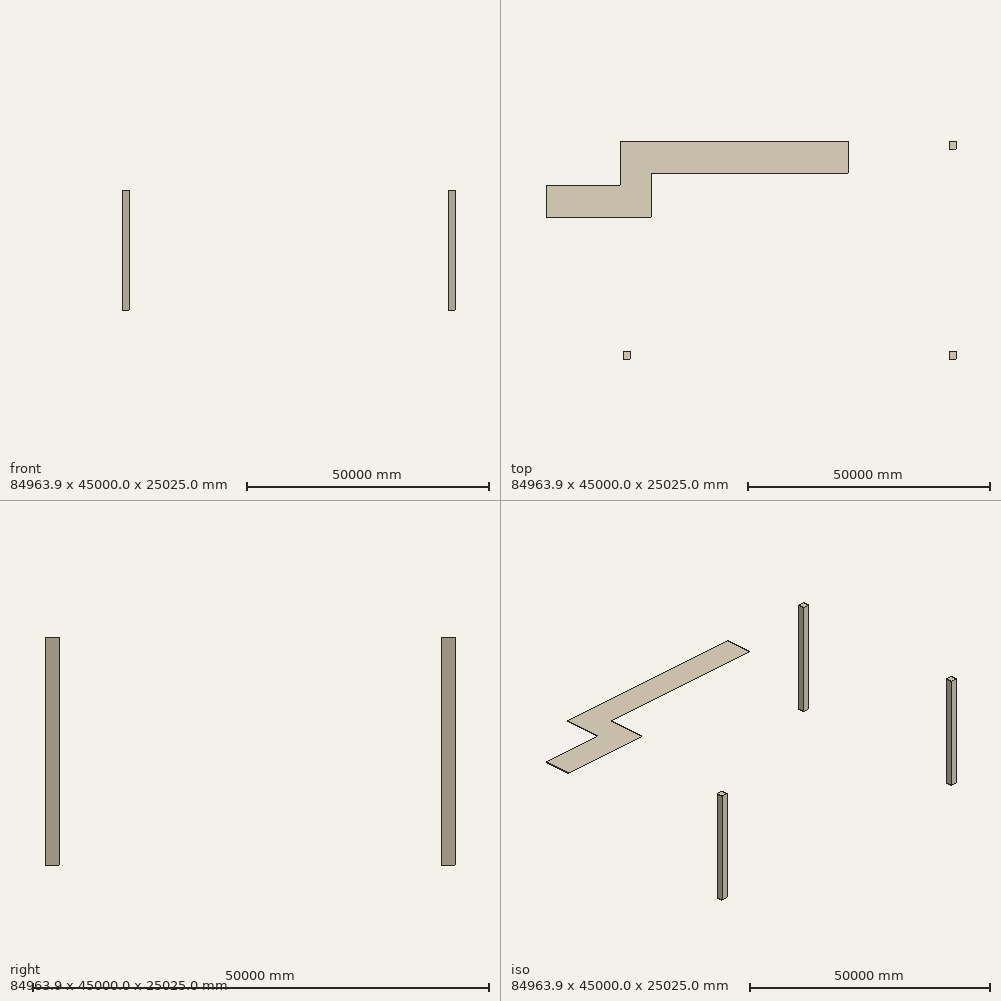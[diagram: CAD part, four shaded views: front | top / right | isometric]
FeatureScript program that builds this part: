
annotation { "Feature Type Name" : "Feature", "Feature Type Description" : "" }
export const myFeature = defineFeature(function(context is Context, id is Id, definition is map)
    precondition{}
    {
        {
            var Q0;
            Q0=qCreatedBy(makeId("Top.planeOp"),FACE);
            var sketch = newSketch(context, id + "F0", { "sketchPlane" : qUnion([Q0])});
            skLineSegment(sketch, "E0.bottom", {"start": v(0, 0) * mm, "end": v(-69700, 0) * mm});
            skLineSegment(sketch, "E0.top", {"start": v(0, 45000) * mm, "end": v(-69700, 45000) * mm});
            skLineSegment(sketch, "E0.left", {"start": v(0, 0) * mm, "end": v(0, 45000) * mm});
            skLineSegment(sketch, "E0.right", {"start": v(-69700, 0) * mm, "end": v(-69700, 45000) * mm});
            skLineSegment(sketch, "E1.bottom", {"start": v(-69700, 45000) * mm, "end": v(-91150.05, 45000) * mm});
            skLineSegment(sketch, "E1.top", {"start": v(-69700, 35900) * mm, "end": v(-91150.05, 35900) * mm});
            skLineSegment(sketch, "E1.left", {"start": v(-69700, 45000) * mm, "end": v(-69700, 35900) * mm});
            skLineSegment(sketch, "E1.right", {"start": v(-91150.05, 45000) * mm, "end": v(-91150.05, 35900) * mm});
            skArc(sketch, "E2", {"start": v(-69700, 34376.03) * mm, "mid": v(-62187.72, 37487.72) * mm, "end": v(-59076.03, 45000) * mm});
            skLineSegment(sketch, "E3", {"start": v(-84963.9, 29400) * mm, "end": v(-63200, 29400) * mm, "construction": true});
            skLineSegment(sketch, "E4", {"start": v(-63200, 29400) * mm, "end": v(-63200, 38500) * mm, "construction": true});
            skLineSegment(sketch, "E5", {"start": v(-63200, 38500) * mm, "end": v(-22400, 38500) * mm, "construction": true});
            skLineSegment(sketch, "E6", {"start": v(-22400, 38500) * mm, "end": v(-22400, 51881.77) * mm, "construction": true});
            skLineSegment(sketch, "E7", {"start": v(-28900, 45000) * mm, "end": v(-28900, 69262.57) * mm});
            skLineSegment(sketch, "E8", {"start": v(-28900, 69262.57) * mm, "end": v(0, 69262.57) * mm});
            skLineSegment(sketch, "E9", {"start": v(0, 69262.57) * mm, "end": v(0, 45000) * mm});
            skSolve(sketch);
        }
        {
            var Q0;
            Q0=qCreatedBy(makeId("Top.planeOp"),FACE);
            var sketch = newSketch(context, id + "F1", { "sketchPlane" : qUnion([Q0])});
            skLineSegment(sketch, "E10.bottom", {"start": v(0, 0) * mm, "end": v(-1200, 0) * mm, "construction": true});
            skLineSegment(sketch, "E10.top", {"start": v(0, 1200) * mm, "end": v(-1200, 1200) * mm, "construction": true});
            skLineSegment(sketch, "E10.left", {"start": v(0, 0) * mm, "end": v(0, 1200) * mm, "construction": true});
            skLineSegment(sketch, "E10.right", {"start": v(-1200, 0) * mm, "end": v(-1200, 1200) * mm, "construction": true});
            skLineSegment(sketch, "E11.bottom", {"start": v(-69700, 0) * mm, "end": v(-68500, 0) * mm});
            skLineSegment(sketch, "E11.top", {"start": v(-69700, 1200) * mm, "end": v(-68500, 1200) * mm});
            skLineSegment(sketch, "E11.left", {"start": v(-69700, 0) * mm, "end": v(-69700, 1200) * mm});
            skLineSegment(sketch, "E11.right", {"start": v(-68500, 0) * mm, "end": v(-68500, 1200) * mm});
            skLineSegment(sketch, "E12.bottom", {"start": v(-28900, 0) * mm, "end": v(-30100, 0) * mm});
            skLineSegment(sketch, "E12.top", {"start": v(-28900, 1200) * mm, "end": v(-30100, 1200) * mm});
            skLineSegment(sketch, "E12.left", {"start": v(-28900, 0) * mm, "end": v(-28900, 1200) * mm});
            skLineSegment(sketch, "E12.right", {"start": v(-30100, 0) * mm, "end": v(-30100, 1200) * mm});
            skLineSegment(sketch, "E13", {"start": v(-28900, 45000) * mm, "end": v(-28900, 1200) * mm, "construction": true});
            skSolve(sketch);
        }
        {
            var Q0;
            Q0=qCreatedBy(makeId("Top.planeOp"),FACE);
            cPlane(context, id + "F2", {"entities" : qUnion([Q0]), "cplaneType" : CPlaneType.OFFSET, "offset" : 25000 * mm, "width" : 150 * mm, "height" : 150 * mm});
        }
        {
            var Q0;
            Q0=qCreatedBy(id+"F2.planeOp",FACE);
            var sketch = newSketch(context, id + "F3", { "sketchPlane" : qUnion([Q0])});
            skLineSegment(sketch, "E14.0", {"start": v(-84963.9, 29400) * mm, "end": v(-63200, 29400) * mm});
            skLineSegment(sketch, "E14.1", {"start": v(-63200, 29400) * mm, "end": v(-63200, 38500) * mm});
            skLineSegment(sketch, "E14.2", {"start": v(-63200, 38500) * mm, "end": v(-22400, 38500) * mm});
            skLineSegment(sketch, "E14.3", {"start": v(-22400, 38500) * mm, "end": v(-22400, 51881.77) * mm});
            skLineSegment(sketch, "E15", {"start": v(-84963.9, 29400) * mm, "end": v(-84963.9, 35900) * mm});
            skLineSegment(sketch, "E16", {"start": v(-84963.9, 35900) * mm, "end": v(-69700, 35900) * mm});
            skLineSegment(sketch, "E17", {"start": v(-69700, 35900) * mm, "end": v(-69700, 45000) * mm});
            skLineSegment(sketch, "E18", {"start": v(-69700, 45000) * mm, "end": v(-22300, 45000) * mm});
            skSolve(sketch);
        }
        {
            var Q0;
            Q0 = qSketchRegion(id + "F3", true);
            extrude(context, id + "F4", {"entities" : qUnion([Q0]), "depth" : 25 * mm, "offsetDistance" : 25 * mm});
        }
        {
            var Q0;
            Q0=qCreatedBy(makeId("Top.planeOp"),FACE);
            var sketch = newSketch(context, id + "F5", { "sketchPlane" : qUnion([Q0])});
            skLineSegment(sketch, "E19.0", {"start": v(0, 0) * mm, "end": v(0, 45000) * mm});
            skLineSegment(sketch, "E19.1", {"start": v(0, 69262.57) * mm, "end": v(0, 45000) * mm});
            skSolve(sketch);
        }
        {
            var Q0;
            Q0 = qSketchRegion(id + "F5", true);
            var Q1;
            Q1=sQuery(id+"F5.wireOp",EDGE,"E19.0");
            var Q2;
            Q2=sQuery(id+"F5.wireOp",EDGE,"E19.1");
            extrude(context, id + "F6", {"entities" : qUnion([Q0]), "bodyType" : ToolBodyType.SURFACE, "surfaceEntities" : qUnion([Q1, Q2]), "depth" : 20000 * mm, "offsetDistance" : 25 * mm});
        }
        {
            var Q0;
            Q0=qCreatedBy(makeId("Top.planeOp"),FACE);
            var sketch = newSketch(context, id + "F7", { "sketchPlane" : qUnion([Q0])});
            skLineSegment(sketch, "E20.bottom", {"start": v(-69100, 45000) * mm, "end": v(-29100, 45000) * mm, "construction": true});
            skLineSegment(sketch, "E20.top", {"start": v(-69100, -5000) * mm, "end": v(-29100, -5000) * mm, "construction": true});
            skLineSegment(sketch, "E20.left", {"start": v(-69100, 45000) * mm, "end": v(-69100, -5000) * mm, "construction": true});
            skLineSegment(sketch, "E20.right", {"start": v(-29100, 45000) * mm, "end": v(-29100, -5000) * mm, "construction": true});
            skLineSegment(sketch, "E21.bottom", {"start": v(-69100, 1500) * mm, "end": v(-67600, 1500) * mm});
            skLineSegment(sketch, "E21.top", {"start": v(-69100, 0) * mm, "end": v(-67600, 0) * mm});
            skLineSegment(sketch, "E21.left", {"start": v(-69100, 1500) * mm, "end": v(-69100, 0) * mm});
            skLineSegment(sketch, "E21.right", {"start": v(-67600, 1500) * mm, "end": v(-67600, 0) * mm});
            skLineSegment(sketch, "E22.bottom", {"start": v(-30600, 1500) * mm, "end": v(-29100, 1500) * mm, "construction": true});
            skLineSegment(sketch, "E22.top", {"start": v(-30600, 0) * mm, "end": v(-29100, 0) * mm, "construction": true});
            skLineSegment(sketch, "E22.left", {"start": v(-30600, 1500) * mm, "end": v(-30600, 0) * mm, "construction": true});
            skLineSegment(sketch, "E22.right", {"start": v(-29100, 1500) * mm, "end": v(-29100, 0) * mm, "construction": true});
            skLineSegment(sketch, "E23.bottom", {"start": v(0, 45000) * mm, "end": v(-1500, 45000) * mm});
            skLineSegment(sketch, "E23.top", {"start": v(0, 43500) * mm, "end": v(-1500, 43500) * mm});
            skLineSegment(sketch, "E23.left", {"start": v(0, 45000) * mm, "end": v(0, 43500) * mm});
            skLineSegment(sketch, "E23.right", {"start": v(-1500, 45000) * mm, "end": v(-1500, 43500) * mm});
            skLineSegment(sketch, "E24.bottom", {"start": v(-1500, 1500) * mm, "end": v(0, 1500) * mm});
            skLineSegment(sketch, "E24.top", {"start": v(-1500, 0) * mm, "end": v(0, 0) * mm});
            skLineSegment(sketch, "E24.left", {"start": v(-1500, 1500) * mm, "end": v(-1500, 0) * mm});
            skLineSegment(sketch, "E24.right", {"start": v(0, 1500) * mm, "end": v(0, 0) * mm});
            skSolve(sketch);
        }
        {
            var Q0;
            Q0=qCreatedBy(makeId("Right.planeOp"),FACE);
            cPlane(context, id + "F8", {"entities" : qUnion([Q0]), "cplaneType" : CPlaneType.OFFSET, "offset" : 28800 * mm, "oppositeDirection" : true, "width" : 150 * mm, "height" : 150 * mm});
        }
        {
            var Q0;
            Q0=qCreatedBy(id+"F8.planeOp",FACE);
            var sketch = newSketch(context, id + "F9", { "sketchPlane" : qUnion([Q0])});
            skLineSegment(sketch, "E25", {"start": v(45000, 0) * mm, "end": v(45000, 23400) * mm, "construction": true});
            skLineSegment(sketch, "E26", {"start": v(45000, 23400) * mm, "end": v(-4824.87, 27581.16) * mm});
            skLineSegment(sketch, "E27", {"start": v(-4824.87, 27581.16) * mm, "end": v(0, 0) * mm, "construction": true});
            skLineSegment(sketch, "E28", {"start": v(0, 0) * mm, "end": v(45000, 0) * mm, "construction": true});
            skSolve(sketch);
        }
        {
            var Q0;
            Q0=qCreatedBy(id+"F8.planeOp",FACE);
            var sketch = newSketch(context, id + "F10", { "sketchPlane" : qUnion([Q0])});
            skLineSegment(sketch, "E29", {"start": v(3256.17, -7650.44) * mm, "end": v(-8438.7, 30601.75) * mm});
            skLineSegment(sketch, "E30", {"start": v(-8438.7, 30601.75) * mm, "end": v(-7004.25, 31040.3) * mm});
            skLineSegment(sketch, "E31", {"start": v(-7004.25, 31040.3) * mm, "end": v(4690.62, -7211.88) * mm});
            skLineSegment(sketch, "E32", {"start": v(4690.62, -7211.88) * mm, "end": v(3256.17, -7650.44) * mm});
            skLineSegment(sketch, "E33.bottom", {"start": v(-1500, 3000) * mm, "end": v(0, 3000) * mm, "construction": true});
            skLineSegment(sketch, "E33.top", {"start": v(-1500, 0) * mm, "end": v(0, 0) * mm, "construction": true});
            skLineSegment(sketch, "E33.left", {"start": v(-1500, 3000) * mm, "end": v(-1500, 0) * mm, "construction": true});
            skLineSegment(sketch, "E33.right", {"start": v(0, 3000) * mm, "end": v(0, 0) * mm, "construction": true});
            skPoint(sketch, "E34.orphan", {"position": v(917.2, 0) * mm});
            skSolve(sketch);
        }
        {
            var Q0;
            Q0=makeQuery(id+"F7.imprint","IMPRINT",FACE,{"disambiguationData":[TD([[makeQuery(id+"F7.imprint","IMPRINT",EDGE,{"derivedFrom":sQuery(id+"F7.wireOp",EDGE,"E23.bottom")}),1.0]])]});
            var Q1;
            Q1=makeQuery(id+"F7.imprint","IMPRINT",FACE,{"disambiguationData":[TD([[makeQuery(id+"F7.imprint","IMPRINT",EDGE,{"derivedFrom":sQuery(id+"F7.wireOp",EDGE,"E24.bottom")}),-1.0]])]});
            var Q2;
            Q2=makeQuery(id+"F7.imprint","IMPRINT",FACE,{"disambiguationData":[TD([[makeQuery(id+"F7.imprint","IMPRINT",EDGE,{"derivedFrom":sQuery(id+"F7.wireOp",EDGE,"E21.bottom")}),-1.0]])]});
            extrude(context, id + "F11", {"entities" : qUnion([Q0, Q1, Q2]), "depth" : 25000 * mm, "offsetDistance" : 25 * mm});
        }
        {
            var Q0;
            Q0=qCreatedBy(makeId("Right.planeOp"),FACE);
            var sketch = newSketch(context, id + "F12", { "sketchPlane" : qUnion([Q0])});
            skLineSegment(sketch, "E35", {"start": v(750, 22500) * mm, "end": v(6187.5, 22500) * mm, "construction": true});
            skLineSegment(sketch, "E36", {"start": v(6187.5, 22500) * mm, "end": v(11625, 22500) * mm, "construction": true});
            skLineSegment(sketch, "E37", {"start": v(11625, 22500) * mm, "end": v(17062.5, 22500) * mm, "construction": true});
            skLineSegment(sketch, "E38", {"start": v(17062.5, 22500) * mm, "end": v(22500, 22500) * mm, "construction": true});
            skLineSegment(sketch, "E39", {"start": v(22500, 22500) * mm, "end": v(27937.5, 22500) * mm, "construction": true});
            skLineSegment(sketch, "E40", {"start": v(27937.5, 22500) * mm, "end": v(33375, 22500) * mm, "construction": true});
            skLineSegment(sketch, "E41", {"start": v(33375, 22500) * mm, "end": v(38812.5, 22500) * mm, "construction": true});
            skLineSegment(sketch, "E42", {"start": v(38812.5, 22500) * mm, "end": v(44250, 22500) * mm, "construction": true});
            skLineSegment(sketch, "E43", {"start": v(750, 25000) * mm, "end": v(750, 22500) * mm, "construction": true});
            skLineSegment(sketch, "E44", {"start": v(44250, 25000) * mm, "end": v(44250, 22500) * mm, "construction": true});
            skArc(sketch, "E45", {"start": v(750, 22500) * mm, "mid": v(3468.75, 21814.44) * mm, "end": v(6187.5, 22500) * mm});
            skArc(sketch, "E46", {"start": v(6187.5, 22500) * mm, "mid": v(8906.25, 21814.44) * mm, "end": v(11625, 22500) * mm});
            skArc(sketch, "E47", {"start": v(11625, 22500) * mm, "mid": v(14343.75, 21814.44) * mm, "end": v(17062.5, 22500) * mm});
            skArc(sketch, "E48", {"start": v(17062.5, 22500) * mm, "mid": v(19781.25, 21814.44) * mm, "end": v(22500, 22500) * mm});
            skArc(sketch, "E49", {"start": v(22500, 22500) * mm, "mid": v(25218.75, 21814.44) * mm, "end": v(27937.5, 22500) * mm});
            skArc(sketch, "E50", {"start": v(27937.5, 22500) * mm, "mid": v(30656.25, 21814.44) * mm, "end": v(33375, 22500) * mm});
            skArc(sketch, "E51", {"start": v(33375, 22500) * mm, "mid": v(36093.75, 21814.44) * mm, "end": v(38812.5, 22500) * mm});
            skArc(sketch, "E52", {"start": v(38812.5, 22500) * mm, "mid": v(41531.25, 21814.44) * mm, "end": v(44250, 22500) * mm});
            skSolve(sketch);
        }
        {
            var Q0;
            Q0 = qSketchRegion(id + "F12", true);
            var Q1;
            Q1=sQuery(id+"F12.wireOp",EDGE,"E51");
            var Q2;
            Q2=sQuery(id+"F12.wireOp",EDGE,"E50");
            var Q3;
            Q3=sQuery(id+"F12.wireOp",EDGE,"E49");
            var Q4;
            Q4=sQuery(id+"F12.wireOp",EDGE,"E52");
            var Q5;
            Q5=sQuery(id+"F12.wireOp",EDGE,"E45");
            var Q6;
            Q6=sQuery(id+"F12.wireOp",EDGE,"E46");
            var Q7;
            Q7=sQuery(id+"F12.wireOp",EDGE,"E48");
            var Q8;
            Q8=sQuery(id+"F12.wireOp",EDGE,"E47");
            var Q9;
            Q9=makeQuery(id+"F4.opExtrude","CAP_VERTEX",VERTEX,{"disambiguationData":[OSD([sQuery(id+"F3.wireOp",EDGE,"E17"),sQuery(id+"F3.wireOp",EDGE,"E18")])],"isStart":true});
            extrude(context, id + "F13", {"entities" : qUnion([Q0]), "bodyType" : ToolBodyType.SURFACE, "surfaceEntities" : qUnion([Q1, Q2, Q3, Q4, Q5, Q6, Q7, Q8]), "endBound" : BoundingType.UP_TO_VERTEX, "oppositeDirection" : true, "depth" : 25 * mm, "endBoundEntityVertex" : qUnion([Q9]), "offsetDistance" : 25 * mm});
        }
    });
